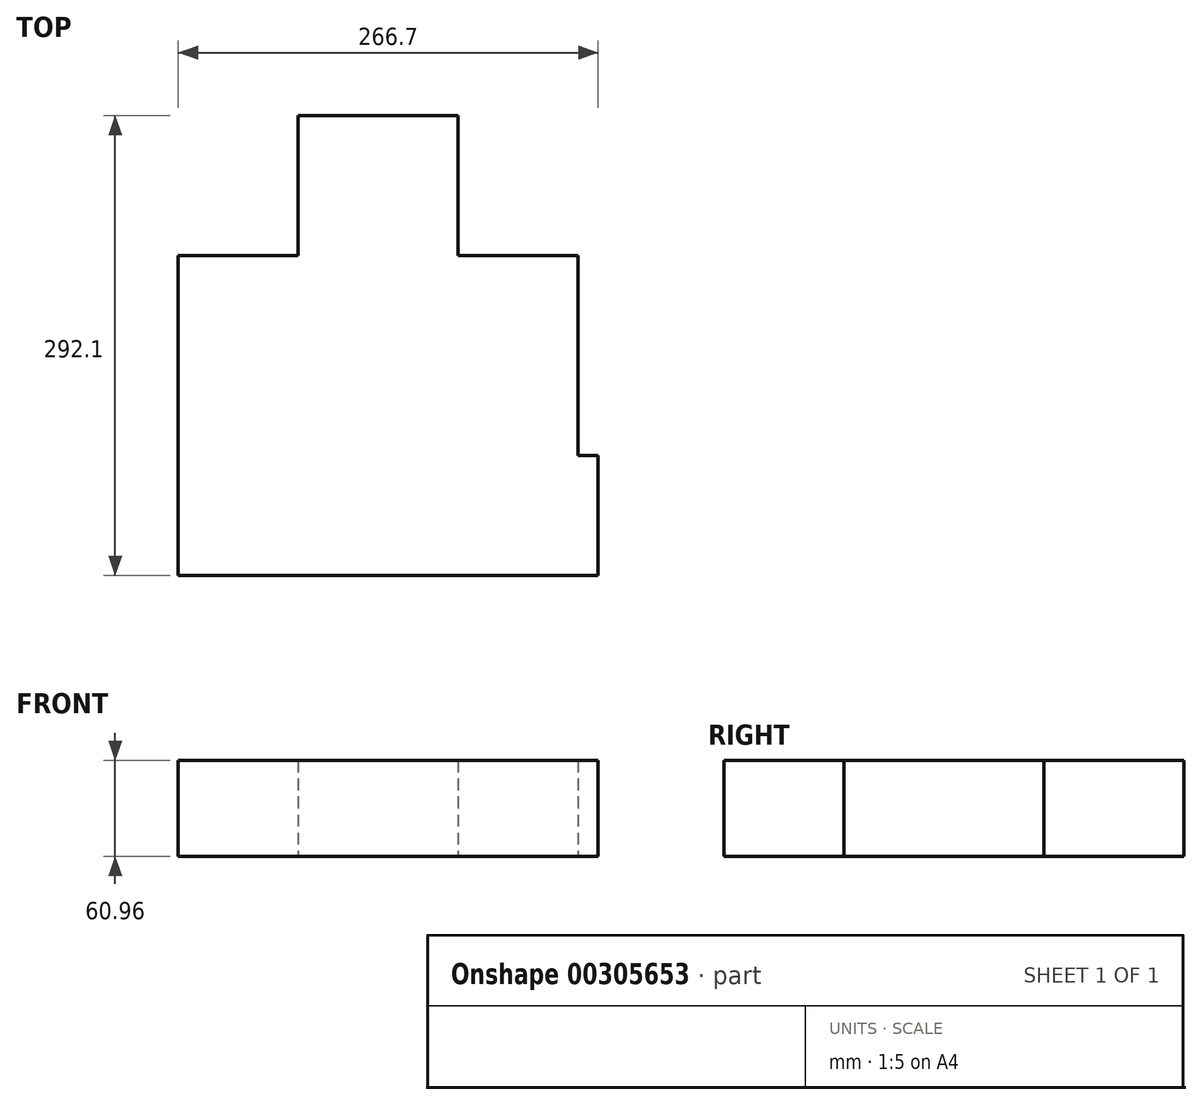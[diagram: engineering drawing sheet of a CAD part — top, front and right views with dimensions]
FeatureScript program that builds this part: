
annotation { "Feature Type Name" : "Feature", "Feature Type Description" : "" }
export const myFeature = defineFeature(function(context is Context, id is Id, definition is map)
    precondition{}
    {
        {
            var Q0;
            Q0=qCreatedBy(makeId("Top.planeOp"),FACE);
            var sketch = newSketch(context, id + "F0", { "sketchPlane" : qUnion([Q0])});
            skLineSegment(sketch, "E0.top", {"start": v(-125.09, -100.2) * mm, "end": v(128.91, -100.2) * mm});
            skLineSegment(sketch, "E0.left", {"start": v(-125.09, 103) * mm, "end": v(-125.09, -100.2) * mm});
            skLineSegment(sketch, "E1.top", {"start": v(-48.89, 191.9) * mm, "end": v(52.71, 191.9) * mm});
            skLineSegment(sketch, "E1.left", {"start": v(-48.89, 103) * mm, "end": v(-48.89, 191.9) * mm});
            skLineSegment(sketch, "E1.right", {"start": v(52.71, 103) * mm, "end": v(52.71, 191.9) * mm});
            skPoint(sketch, "E2", {"position": v(-48.89, 103) * mm});
            skPoint(sketch, "E3", {"position": v(52.71, 103) * mm});
            skPoint(sketch, "E4", {"position": v(128.91, -24) * mm});
            skLineSegment(sketch, "E5", {"start": v(128.91, -24) * mm, "end": v(141.61, -24) * mm});
            skLineSegment(sketch, "E6", {"start": v(141.61, -24) * mm, "end": v(141.61, -100.2) * mm});
            skLineSegment(sketch, "E7", {"start": v(141.61, -100.2) * mm, "end": v(128.91, -100.2) * mm});
            skLineSegment(sketch, "E8", {"start": v(128.91, -24) * mm, "end": v(128.91, 103) * mm});
            skLineSegment(sketch, "E9", {"start": v(-48.89, 103) * mm, "end": v(-125.09, 103) * mm});
            skLineSegment(sketch, "E10", {"start": v(52.71, 103) * mm, "end": v(128.91, 103) * mm});
            skLineSegment(sketch, "E11", {"start": v(-48.89, 103) * mm, "end": v(-48.89, -24) * mm});
            skLineSegment(sketch, "E12", {"start": v(-48.89, -24) * mm, "end": v(-125.09, -24) * mm});
            skLineSegment(sketch, "E13.bottom", {"start": v(128.91, -24) * mm, "end": v(65.41, -24) * mm});
            skLineSegment(sketch, "E13.top", {"start": v(128.91, -3.67) * mm, "end": v(65.41, -3.67) * mm});
            skLineSegment(sketch, "E13.left", {"start": v(128.91, -24) * mm, "end": v(128.91, -3.67) * mm});
            skLineSegment(sketch, "E13.right", {"start": v(65.41, -24) * mm, "end": v(65.41, -3.67) * mm});
            skLineSegment(sketch, "E14", {"start": v(-48.89, -24) * mm, "end": v(1.91, -24) * mm});
            skLineSegment(sketch, "E15", {"start": v(1.91, -24) * mm, "end": v(1.91, 64.9) * mm});
            skLineSegment(sketch, "E16", {"start": v(1.91, 64.9) * mm, "end": v(-48.89, 64.9) * mm});
            skLineSegment(sketch, "E17.bottom", {"start": v(-23.49, -100.2) * mm, "end": v(67.95, -100.2) * mm});
            skLineSegment(sketch, "E17.top", {"start": v(-23.49, -59.55) * mm, "end": v(67.95, -59.55) * mm});
            skLineSegment(sketch, "E17.left", {"start": v(-23.49, -100.2) * mm, "end": v(-23.49, -59.55) * mm});
            skLineSegment(sketch, "E17.right", {"start": v(67.95, -100.2) * mm, "end": v(67.95, -59.55) * mm});
            skLineSegment(sketch, "E18", {"start": v(60.33, -59.55) * mm, "end": v(60.33, -100.2) * mm});
            skLineSegment(sketch, "E19.MirrorCS", {"start": v(52.71, -100.2) * mm, "end": v(52.71, -59.55) * mm});
            skLineSegment(sketch, "E20.MirrorCS", {"start": v(45.1, -59.55) * mm, "end": v(45.1, -100.2) * mm});
            skLineSegment(sketch, "E21.MirrorCS", {"start": v(37.47, -100.2) * mm, "end": v(37.47, -59.55) * mm});
            skLineSegment(sketch, "E22.MirrorCS", {"start": v(14.61, -59.55) * mm, "end": v(14.61, -100.2) * mm});
            skLineSegment(sketch, "E23.MirrorCS", {"start": v(22.23, -100.2) * mm, "end": v(22.23, -59.55) * mm});
            skLineSegment(sketch, "E24.MirrorCS", {"start": v(29.85, -59.55) * mm, "end": v(29.85, -100.2) * mm});
            skLineSegment(sketch, "E25.MirrorCS", {"start": v(-8.25, -100.2) * mm, "end": v(-8.25, -59.55) * mm});
            skLineSegment(sketch, "E26.MirrorCS", {"start": v(-0.63, -59.55) * mm, "end": v(-0.63, -100.2) * mm});
            skLineSegment(sketch, "E27.MirrorCS", {"start": v(7, -100.2) * mm, "end": v(7, -59.55) * mm});
            skLineSegment(sketch, "E28.MirrorCS", {"start": v(-15.87, -59.55) * mm, "end": v(-15.87, -100.2) * mm});
            skSolve(sketch);
        }
        {
            var Q0;
            Q0=makeQuery(id+"F0.imprint","IMPRINT",FACE,{"disambiguationData":[TD([[makeQuery(id+"F0.imprint","IMPRINT",EDGE,{"derivedFrom":sQuery(id+"F0.wireOp",EDGE,"E1.top")}),-1.0]])]});
            var Q1;
            {var subQ0=sQuery(id+"F0.wireOp",EDGE,"E18");Q1=makeQuery(id+"F0.imprint","IMPRINT",FACE,{"disambiguationData":[TD([[makeQuery(id+"F0.imprint","IMPRINT",EDGE,{"derivedFrom":subQ0}),-1.0]])]});}
            var Q2;
            {var subQ0=sQuery(id+"F0.wireOp",EDGE,"E20.MirrorCS");Q2=makeQuery(id+"F0.imprint","IMPRINT",FACE,{"disambiguationData":[TD([[makeQuery(id+"F0.imprint","IMPRINT",EDGE,{"derivedFrom":subQ0}),1.0]])]});}
            var Q3;
            Q3=makeQuery(id+"F0.imprint","IMPRINT",FACE,{"disambiguationData":[TD([[makeQuery(id+"F0.imprint","IMPRINT",EDGE,{"derivedFrom":sQuery(id+"F0.wireOp",EDGE,"E13.bottom")}),-1.0]])]});
            var Q4;
            {var subQ3=sQuery(id+"F0.wireOp",EDGE,"E9");Q4=makeQuery(id+"F0.imprint","IMPRINT",FACE,{"disambiguationData":[TD([[makeQuery(id+"F0.imprint","IMPRINT",EDGE,{"derivedFrom":subQ3}),1.0]])]});}
            var Q5;
            {var subQ0=sQuery(id+"F0.wireOp",EDGE,"E17.left");Q5=makeQuery(id+"F0.imprint","IMPRINT",FACE,{"disambiguationData":[TD([[makeQuery(id+"F0.imprint","IMPRINT",EDGE,{"derivedFrom":subQ0}),-1.0]])]});}
            var Q6;
            {var subQ2=sQuery(id+"F0.wireOp",EDGE,"E18");Q6=makeQuery(id+"F0.imprint","IMPRINT",FACE,{"disambiguationData":[TD([[makeQuery(id+"F0.imprint","IMPRINT",EDGE,{"derivedFrom":subQ2}),1.0]])]});}
            var Q7;
            {var subQ0=sQuery(id+"F0.wireOp",EDGE,"E25.MirrorCS");Q7=makeQuery(id+"F0.imprint","IMPRINT",FACE,{"disambiguationData":[TD([[makeQuery(id+"F0.imprint","IMPRINT",EDGE,{"derivedFrom":subQ0}),1.0]])]});}
            var Q8;
            {var subQ0=sQuery(id+"F0.wireOp",EDGE,"E25.MirrorCS");Q8=makeQuery(id+"F0.imprint","IMPRINT",FACE,{"disambiguationData":[TD([[makeQuery(id+"F0.imprint","IMPRINT",EDGE,{"derivedFrom":subQ0}),-1.0]])]});}
            var Q9;
            {var subQ0=sQuery(id+"F0.wireOp",EDGE,"E26.MirrorCS");Q9=makeQuery(id+"F0.imprint","IMPRINT",FACE,{"disambiguationData":[TD([[makeQuery(id+"F0.imprint","IMPRINT",EDGE,{"derivedFrom":subQ0}),1.0]])]});}
            var Q10;
            {var subQ0=sQuery(id+"F0.wireOp",EDGE,"E20.MirrorCS");Q10=makeQuery(id+"F0.imprint","IMPRINT",FACE,{"disambiguationData":[TD([[makeQuery(id+"F0.imprint","IMPRINT",EDGE,{"derivedFrom":subQ0}),-1.0]])]});}
            var Q11;
            {var subQ0=sQuery(id+"F0.wireOp",EDGE,"E21.MirrorCS");Q11=makeQuery(id+"F0.imprint","IMPRINT",FACE,{"disambiguationData":[TD([[makeQuery(id+"F0.imprint","IMPRINT",EDGE,{"derivedFrom":subQ0}),1.0]])]});}
            var Q12;
            {var subQ0=sQuery(id+"F0.wireOp",EDGE,"E23.MirrorCS");Q12=makeQuery(id+"F0.imprint","IMPRINT",FACE,{"disambiguationData":[TD([[makeQuery(id+"F0.imprint","IMPRINT",EDGE,{"derivedFrom":subQ0}),-1.0]])]});}
            var Q13;
            {var subQ0=sQuery(id+"F0.wireOp",EDGE,"E22.MirrorCS");Q13=makeQuery(id+"F0.imprint","IMPRINT",FACE,{"disambiguationData":[TD([[makeQuery(id+"F0.imprint","IMPRINT",EDGE,{"derivedFrom":subQ0}),-1.0]])]});}
            var Q14;
            {var subQ0=sQuery(id+"F0.wireOp",EDGE,"E22.MirrorCS");Q14=makeQuery(id+"F0.imprint","IMPRINT",FACE,{"disambiguationData":[TD([[makeQuery(id+"F0.imprint","IMPRINT",EDGE,{"derivedFrom":subQ0}),1.0]])]});}
            var Q15;
            {var subQ0=sQuery(id+"F0.wireOp",EDGE,"E14");Q15=makeQuery(id+"F0.imprint","IMPRINT",FACE,{"disambiguationData":[TD([[makeQuery(id+"F0.imprint","IMPRINT",EDGE,{"derivedFrom":subQ0}),1.0]])]});}
            extrude(context, id + "F1", {"entities" : qUnion([Q0, Q1, Q2, Q3, Q4, Q5, Q6, Q7, Q8, Q9, Q10, Q11, Q12, Q13, Q14, Q15]), "depth" : 60.96 * mm});
        }
    });
